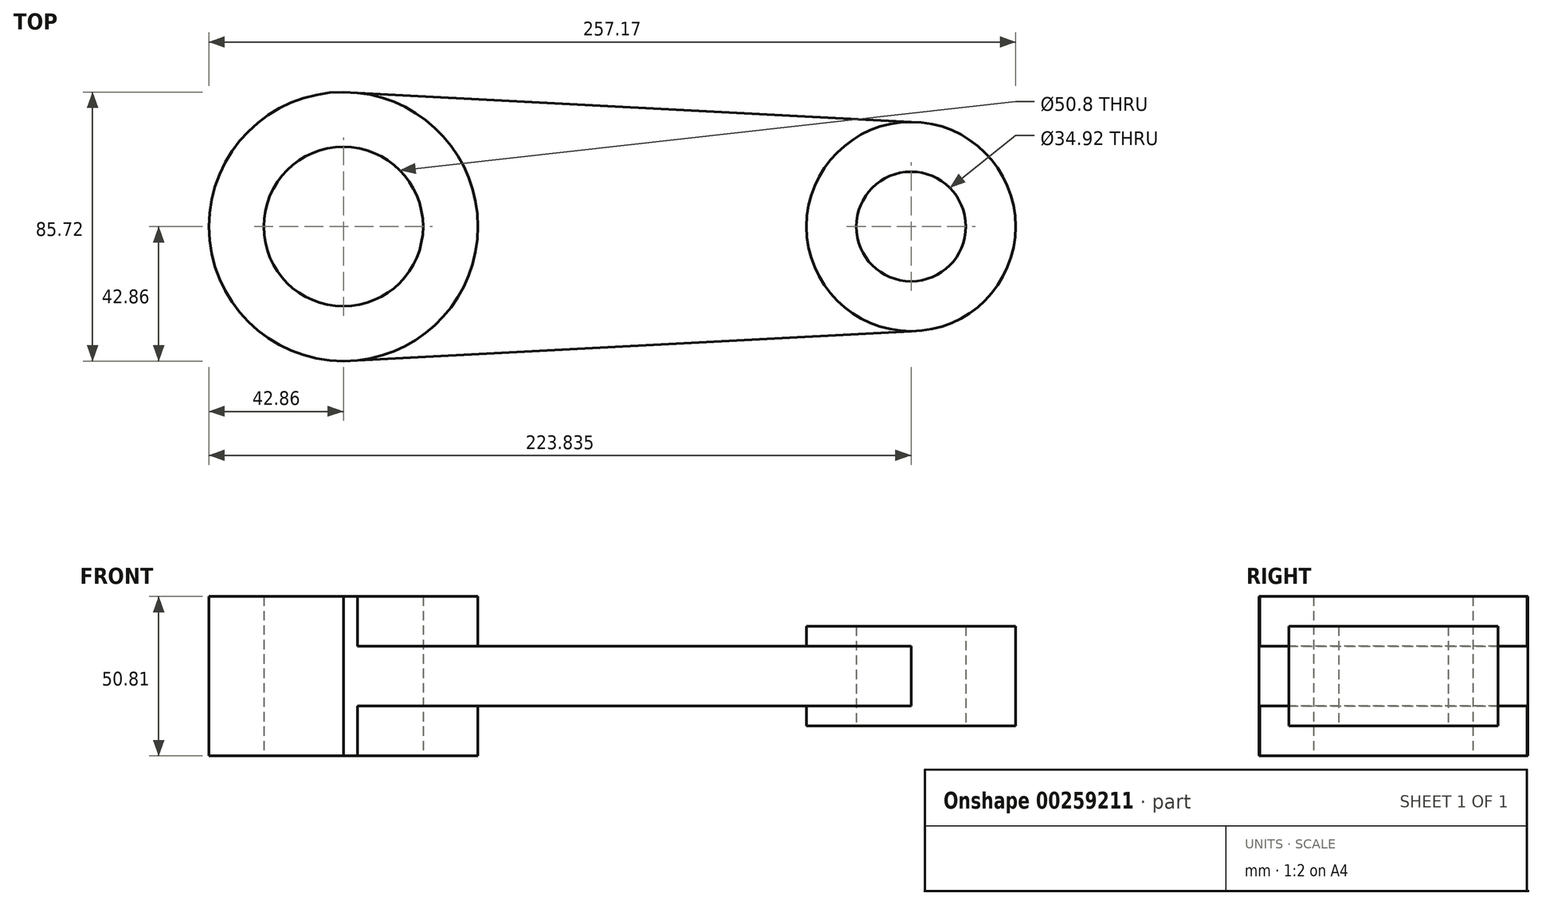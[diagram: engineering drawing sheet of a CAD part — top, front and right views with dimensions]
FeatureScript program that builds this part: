
annotation { "Feature Type Name" : "Feature", "Feature Type Description" : "" }
export const myFeature = defineFeature(function(context is Context, id is Id, definition is map)
    precondition{}
    {
        {
            var Q0;
            Q0=qCreatedBy(makeId("Top.planeOp"),FACE);
            var sketch = newSketch(context, id + "F0", { "sketchPlane" : qUnion([Q0])});
            skCircle(sketch, "E0", {"center": v(0, 0) * mm, "radius": 42.86 * mm});
            skCircle(sketch, "E1", {"center": v(180.98, 0) * mm, "radius": 33.34 * mm});
            skLineSegment(sketch, "E2", {"start": v(0, 0) * mm, "end": v(180.98, 0) * mm});
            skLineSegment(sketch, "E3", {"start": v(0, 42.86) * mm, "end": v(180.97, 33.34) * mm});
            skLineSegment(sketch, "E4", {"start": v(180.97, 33.34) * mm, "end": v(180.97, -33.34) * mm});
            skLineSegment(sketch, "E5", {"start": v(0, 42.86) * mm, "end": v(0, -42.86) * mm});
            skLineSegment(sketch, "E6", {"start": v(0, -42.86) * mm, "end": v(180.97, -33.34) * mm});
            skCircle(sketch, "E7", {"center": v(0, 0) * mm, "radius": 25.4 * mm});
            skCircle(sketch, "E8", {"center": v(180.98, 0) * mm, "radius": 17.46 * mm});
            skSolve(sketch);
        }
        {
            var Q0;
            {var subQ1=sQuery(id+"F0.wireOp",EDGE,"E3");var subQ2=sQuery(id+"F0.wireOp",EDGE,"E0");var subQ6=makeQuery(id+"F0.imprint","INTERSECT",VERTEX,{"derivedFrom":[subQ2,subQ1]});Q0=makeQuery(id+"F0.imprint","IMPRINT",FACE,{"disambiguationData":[TD([[makeQuery(id+"F0.imprint","IMPRINT",EDGE,{"disambiguationData":[TD([[subQ6,1.0]])],"derivedFrom":subQ2}),1.0]])]});}
            var Q1;
            {var subQ0=sQuery(id+"F0.wireOp",EDGE,"E5");var subQ4=sQuery(id+"F0.wireOp",EDGE,"E7");var subQ5=makeQuery(id+"F0.imprint","INTERSECT",VERTEX,{"disambiguationData":[OD(0.0)],"derivedFrom":[subQ0,subQ4]});Q1=makeQuery(id+"F0.imprint","IMPRINT",FACE,{"disambiguationData":[TD([[makeQuery(id+"F0.imprint","IMPRINT",EDGE,{"disambiguationData":[TD([[subQ5,-1.0]])],"derivedFrom":subQ4}),-1.0]])]});}
            var Q2;
            {var subQ0=sQuery(id+"F0.wireOp",EDGE,"E6");var subQ2=sQuery(id+"F0.wireOp",EDGE,"E0");var subQ4=makeQuery(id+"F0.imprint","INTERSECT",VERTEX,{"derivedFrom":[subQ2,subQ0]});Q2=makeQuery(id+"F0.imprint","IMPRINT",FACE,{"disambiguationData":[TD([[makeQuery(id+"F0.imprint","IMPRINT",EDGE,{"disambiguationData":[TD([[subQ4,-1.0]])],"derivedFrom":subQ2}),1.0]])]});}
            var Q3;
            {var subQ0=sQuery(id+"F0.wireOp",EDGE,"E3");var subQ1=sQuery(id+"F0.wireOp",EDGE,"E0");var subQ2=makeQuery(id+"F0.imprint","INTERSECT",VERTEX,{"derivedFrom":[subQ1,subQ0]});Q3=makeQuery(id+"F0.imprint","IMPRINT",FACE,{"disambiguationData":[TD([[makeQuery(id+"F0.imprint","IMPRINT",EDGE,{"disambiguationData":[TD([[subQ2,1.0]])],"derivedFrom":subQ1}),-1.0]])]});}
            var Q4;
            {var subQ0=sQuery(id+"F0.wireOp",EDGE,"E6");var subQ1=sQuery(id+"F0.wireOp",EDGE,"E0");var subQ2=makeQuery(id+"F0.imprint","INTERSECT",VERTEX,{"derivedFrom":[subQ1,subQ0]});Q4=makeQuery(id+"F0.imprint","IMPRINT",FACE,{"disambiguationData":[TD([[makeQuery(id+"F0.imprint","IMPRINT",EDGE,{"disambiguationData":[TD([[subQ2,-1.0]])],"derivedFrom":subQ1}),-1.0]])]});}
            var Q5;
            {var subQ1=sQuery(id+"F0.wireOp",EDGE,"E1");var subQ3=sQuery(id+"F0.wireOp",EDGE,"E2");var subQ4=makeQuery(id+"F0.imprint","INTERSECT",VERTEX,{"derivedFrom":[subQ1,subQ3]});Q5=makeQuery(id+"F0.imprint","IMPRINT",FACE,{"disambiguationData":[TD([[makeQuery(id+"F0.imprint","IMPRINT",EDGE,{"disambiguationData":[TD([[subQ4,-1.0]])],"derivedFrom":subQ3}),1.0]])]});}
            var Q6;
            {var subQ1=sQuery(id+"F0.wireOp",EDGE,"E1");var subQ3=sQuery(id+"F0.wireOp",EDGE,"E2");var subQ4=makeQuery(id+"F0.imprint","INTERSECT",VERTEX,{"derivedFrom":[subQ1,subQ3]});Q6=makeQuery(id+"F0.imprint","IMPRINT",FACE,{"disambiguationData":[TD([[makeQuery(id+"F0.imprint","IMPRINT",EDGE,{"disambiguationData":[TD([[subQ4,-1.0]])],"derivedFrom":subQ3}),-1.0]])]});}
            var Q7;
            {var subQ0=sQuery(id+"F0.wireOp",EDGE,"E4");var subQ4=sQuery(id+"F0.wireOp",EDGE,"E8");var subQ5=makeQuery(id+"F0.imprint","INTERSECT",VERTEX,{"disambiguationData":[OD(0.0)],"derivedFrom":[subQ0,subQ4]});Q7=makeQuery(id+"F0.imprint","IMPRINT",FACE,{"disambiguationData":[TD([[makeQuery(id+"F0.imprint","IMPRINT",EDGE,{"disambiguationData":[TD([[subQ5,1.0]])],"derivedFrom":subQ4}),-1.0]])]});}
            extrude(context, id + "F1", {"entities" : qUnion([Q0, Q1, Q2, Q3, Q4, Q5, Q6, Q7]), "depth" : 19.05 * mm});
        }
        {
            var Q0;
            {var subQ0=sQuery(id+"F0.wireOp",EDGE,"E6");var subQ2=sQuery(id+"F0.wireOp",EDGE,"E0");var subQ4=makeQuery(id+"F0.imprint","INTERSECT",VERTEX,{"derivedFrom":[subQ2,subQ0]});Q0=makeQuery(id+"F0.imprint","IMPRINT",FACE,{"disambiguationData":[TD([[makeQuery(id+"F0.imprint","IMPRINT",EDGE,{"disambiguationData":[TD([[subQ4,-1.0]])],"derivedFrom":subQ2}),1.0]])]});}
            var Q1;
            {var subQ0=sQuery(id+"F0.wireOp",EDGE,"E5");var subQ4=sQuery(id+"F0.wireOp",EDGE,"E7");var subQ5=makeQuery(id+"F0.imprint","INTERSECT",VERTEX,{"disambiguationData":[OD(0.0)],"derivedFrom":[subQ0,subQ4]});Q1=makeQuery(id+"F0.imprint","IMPRINT",FACE,{"disambiguationData":[TD([[makeQuery(id+"F0.imprint","IMPRINT",EDGE,{"disambiguationData":[TD([[subQ5,-1.0]])],"derivedFrom":subQ4}),-1.0]])]});}
            var Q2;
            {var subQ1=sQuery(id+"F0.wireOp",EDGE,"E3");var subQ2=sQuery(id+"F0.wireOp",EDGE,"E0");var subQ6=makeQuery(id+"F0.imprint","INTERSECT",VERTEX,{"derivedFrom":[subQ2,subQ1]});Q2=makeQuery(id+"F0.imprint","IMPRINT",FACE,{"disambiguationData":[TD([[makeQuery(id+"F0.imprint","IMPRINT",EDGE,{"disambiguationData":[TD([[subQ6,1.0]])],"derivedFrom":subQ2}),1.0]])]});}
            extrude(context, id + "F2", {"entities" : qUnion([Q0, Q1, Q2]), "operationType" : NewBodyOperationType.ADD, "oppositeDirection" : true, "depth" : 15.88 * mm, "hasSecondDirection" : true, "secondDirectionOppositeDirection" : false, "secondDirectionDepth" : 34.92 * mm});
        }
        {
            var Q0;
            {var subQ0=sQuery(id+"F0.wireOp",EDGE,"E4");var subQ4=sQuery(id+"F0.wireOp",EDGE,"E8");var subQ5=makeQuery(id+"F0.imprint","INTERSECT",VERTEX,{"disambiguationData":[OD(0.0)],"derivedFrom":[subQ0,subQ4]});Q0=makeQuery(id+"F0.imprint","IMPRINT",FACE,{"disambiguationData":[TD([[makeQuery(id+"F0.imprint","IMPRINT",EDGE,{"disambiguationData":[TD([[subQ5,1.0]])],"derivedFrom":subQ4}),-1.0]])]});}
            var Q1;
            {var subQ1=sQuery(id+"F0.wireOp",EDGE,"E1");var subQ3=sQuery(id+"F0.wireOp",EDGE,"E2");var subQ4=makeQuery(id+"F0.imprint","INTERSECT",VERTEX,{"derivedFrom":[subQ1,subQ3]});Q1=makeQuery(id+"F0.imprint","IMPRINT",FACE,{"disambiguationData":[TD([[makeQuery(id+"F0.imprint","IMPRINT",EDGE,{"disambiguationData":[TD([[subQ4,-1.0]])],"derivedFrom":subQ3}),-1.0]])]});}
            var Q2;
            {var subQ1=sQuery(id+"F0.wireOp",EDGE,"E1");var subQ3=sQuery(id+"F0.wireOp",EDGE,"E2");var subQ4=makeQuery(id+"F0.imprint","INTERSECT",VERTEX,{"derivedFrom":[subQ1,subQ3]});Q2=makeQuery(id+"F0.imprint","IMPRINT",FACE,{"disambiguationData":[TD([[makeQuery(id+"F0.imprint","IMPRINT",EDGE,{"disambiguationData":[TD([[subQ4,-1.0]])],"derivedFrom":subQ3}),1.0]])]});}
            extrude(context, id + "F3", {"entities" : qUnion([Q0, Q1, Q2]), "operationType" : NewBodyOperationType.ADD, "depth" : 25.4 * mm, "hasSecondDirection" : true, "secondDirectionOppositeDirection" : true, "secondDirectionDepth" : 6.35 * mm});
        }
    });
